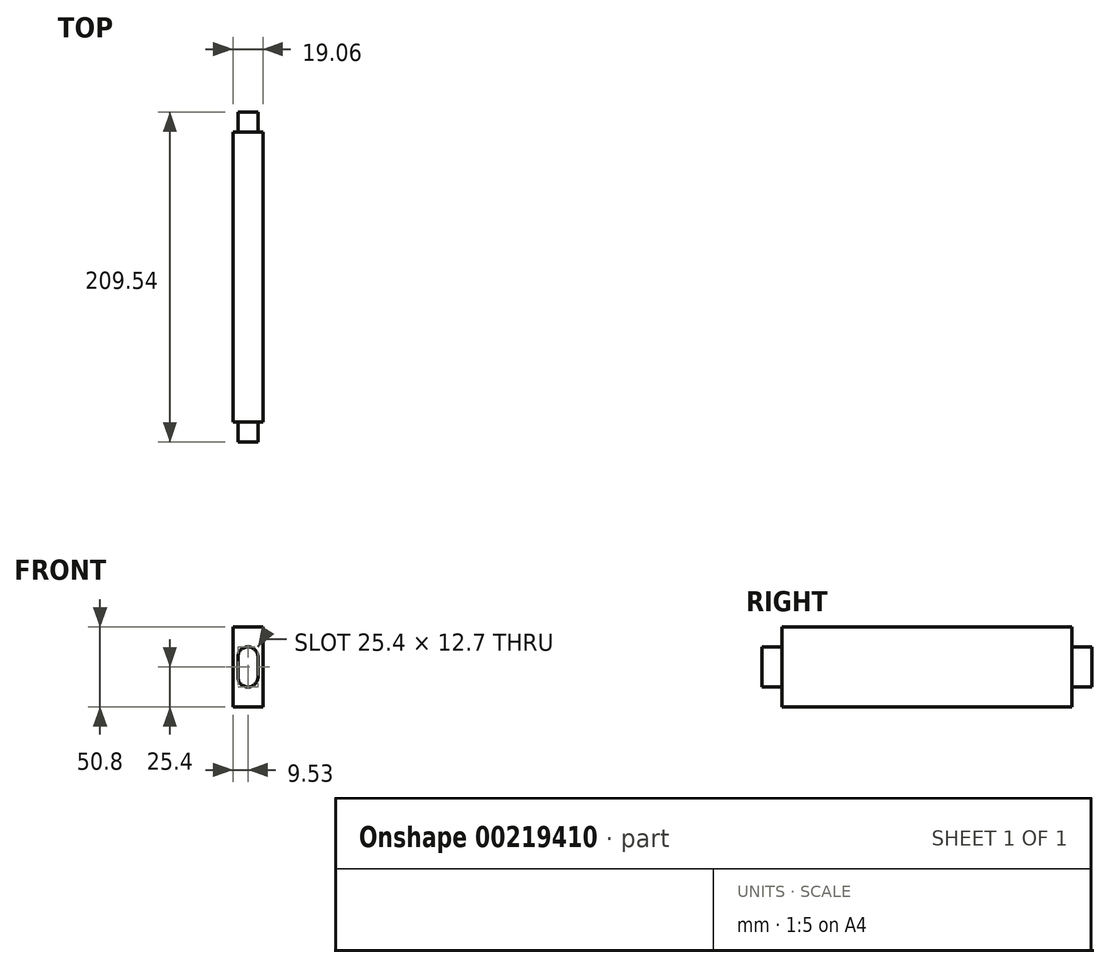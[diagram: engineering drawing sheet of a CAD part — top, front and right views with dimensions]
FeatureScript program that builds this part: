
annotation { "Feature Type Name" : "Feature", "Feature Type Description" : "" }
export const myFeature = defineFeature(function(context is Context, id is Id, definition is map)
    precondition{}
    {
        {
            var Q0;
            Q0=qCreatedBy(makeId("Top.planeOp"),FACE);
            var sketch = newSketch(context, id + "F0", { "sketchPlane" : qUnion([Q0])});
            skLineSegment(sketch, "E0.bottom", {"start": v(-9.53, -92.08) * mm, "end": v(9.52, -92.08) * mm});
            skLineSegment(sketch, "E0.top", {"start": v(-9.53, 92.07) * mm, "end": v(9.52, 92.07) * mm});
            skLineSegment(sketch, "E0.left", {"start": v(-9.53, -92.08) * mm, "end": v(-9.53, 92.07) * mm});
            skLineSegment(sketch, "E0.right", {"start": v(9.52, -92.08) * mm, "end": v(9.52, 92.07) * mm});
            skPoint(sketch, "E0.middle", {"position": v(0, 0) * mm});
            skSolve(sketch);
        }
        {
            var Q0;
            Q0=qSketchRegion(id+"F0",true);
            extrude(context, id + "F1", {"entities" : qUnion([Q0]), "oppositeDirection" : true, "depth" : 50.8 * mm, "offsetDistance" : 25.4 * mm});
        }
        {
            var Q0;
            Q0=makeQuery(id+"F1.opExtrude","SWEPT_FACE",FACE,{"disambiguationData":[OSD([sQuery(id+"F0.wireOp",EDGE,"E0.bottom")])]});
            var sketch = newSketch(context, id + "F2", { "sketchPlane" : qUnion([Q0])});
            skLineSegment(sketch, "E1.bottom", {"start": v(-6.35, -38.1) * mm, "end": v(6.35, -38.1) * mm});
            skLineSegment(sketch, "E1.top", {"start": v(-6.35, -12.7) * mm, "end": v(6.35, -12.7) * mm});
            skLineSegment(sketch, "E1.left", {"start": v(-6.35, -38.1) * mm, "end": v(-6.35, -12.7) * mm});
            skLineSegment(sketch, "E1.right", {"start": v(6.35, -38.1) * mm, "end": v(6.35, -12.7) * mm});
            skPoint(sketch, "E1.middle", {"position": v(0, -25.4) * mm});
            skSolve(sketch);
        }
        {
            var Q0;
            Q0=qSketchRegion(id+"F2",true);
            extrude(context, id + "F3", {"entities" : qUnion([Q0]), "operationType" : NewBodyOperationType.ADD, "depth" : 12.7 * mm, "offsetDistance" : 25.4 * mm});
        }
        {
            var Q0;
            Q0=makeQuery(id+"F1.opExtrude","SWEPT_FACE",FACE,{"disambiguationData":[OSD([sQuery(id+"F0.wireOp",EDGE,"E0.top")])]});
            var sketch = newSketch(context, id + "F4", { "sketchPlane" : qUnion([Q0])});
            skLineSegment(sketch, "E2.bottom", {"start": v(-6.35, -38.1) * mm, "end": v(6.35, -38.1) * mm});
            skLineSegment(sketch, "E2.top", {"start": v(-6.35, -12.7) * mm, "end": v(6.35, -12.7) * mm});
            skLineSegment(sketch, "E2.left", {"start": v(-6.35, -38.1) * mm, "end": v(-6.35, -12.7) * mm});
            skLineSegment(sketch, "E2.right", {"start": v(6.35, -38.1) * mm, "end": v(6.35, -12.7) * mm});
            skPoint(sketch, "E2.middle", {"position": v(0, -25.4) * mm});
            skSolve(sketch);
        }
        {
            var Q0;
            Q0=qSketchRegion(id+"F4",true);
            extrude(context, id + "F5", {"entities" : qUnion([Q0]), "operationType" : NewBodyOperationType.ADD, "depth" : 12.7 * mm, "offsetDistance" : 25.4 * mm});
        }
        {
            var Q0;
            Q0=makeQuery(id+"F5.opExtrude","SWEPT_EDGE",EDGE,{"disambiguationData":[OSD([sQuery(id+"F4.wireOp",EDGE,"E2.top"),sQuery(id+"F4.wireOp",EDGE,"E2.left")])]});
            var Q1;
            Q1=makeQuery(id+"F5.opExtrude","SWEPT_EDGE",EDGE,{"disambiguationData":[OSD([sQuery(id+"F4.wireOp",EDGE,"E2.top"),sQuery(id+"F4.wireOp",EDGE,"E2.right")])]});
            var Q2;
            Q2=makeQuery(id+"F5.opExtrude","SWEPT_EDGE",EDGE,{"disambiguationData":[OSD([sQuery(id+"F4.wireOp",EDGE,"E2.bottom"),sQuery(id+"F4.wireOp",EDGE,"E2.right")])]});
            var Q3;
            Q3=makeQuery(id+"F5.opExtrude","SWEPT_EDGE",EDGE,{"disambiguationData":[OSD([sQuery(id+"F4.wireOp",EDGE,"E2.bottom"),sQuery(id+"F4.wireOp",EDGE,"E2.left")])]});
            var Q4;
            Q4=makeQuery(id+"F3.opExtrude","SWEPT_EDGE",EDGE,{"disambiguationData":[OSD([sQuery(id+"F2.wireOp",EDGE,"E1.top"),sQuery(id+"F2.wireOp",EDGE,"E1.left")])]});
            var Q5;
            Q5=makeQuery(id+"F3.opExtrude","SWEPT_EDGE",EDGE,{"disambiguationData":[OSD([sQuery(id+"F2.wireOp",EDGE,"E1.top"),sQuery(id+"F2.wireOp",EDGE,"E1.right")])]});
            var Q6;
            Q6=makeQuery(id+"F3.opExtrude","SWEPT_EDGE",EDGE,{"disambiguationData":[OSD([sQuery(id+"F2.wireOp",EDGE,"E1.bottom"),sQuery(id+"F2.wireOp",EDGE,"E1.left")])]});
            var Q7;
            Q7=makeQuery(id+"F3.opExtrude","SWEPT_EDGE",EDGE,{"disambiguationData":[OSD([sQuery(id+"F2.wireOp",EDGE,"E1.bottom"),sQuery(id+"F2.wireOp",EDGE,"E1.right")])]});
            fillet(context, id + "F6", {"entities" : qUnion([Q0, Q1, Q2, Q3, Q4, Q5, Q6, Q7]), "radius" : 6.35 * mm, "tangentPropagation" : true, "allowEdgeOverflow" : false});
        }
    });
